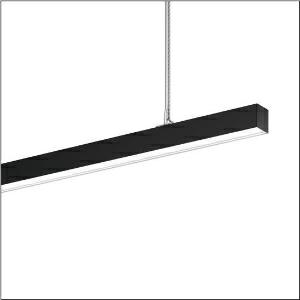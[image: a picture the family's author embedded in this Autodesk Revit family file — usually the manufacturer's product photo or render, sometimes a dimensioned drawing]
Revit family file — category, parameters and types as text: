
# Revit family: silica_r__21_51mx30da44bb_2b52
name_source: partatom
category: Lighting Fixtures
units: mm (PartAtom-declared; Revit-internal decimal feet)

## family parameters
Cut with Voids When Loaded = No
Host = Face
Light Source = No
Part Type = Normal
Room Calculation Point = No
Round Connector Dimension = Use Diameter
Shared = No

## types (1)
- --- (1 x LED, 4210 lm, 26 W, 4000K)
    Apparent Load = 26 VA
    CIE Flux Codes = 47 79 96 57 100
    Color Rendering = 80
    Color Temperature = 4000K
    Default Elevation = 1800 mm
    Description = Silica® 21, office luminaire, primary optical cover: cover, of PMMA, opal, light emission: direct/indirect distribution, primary light characteristic: symmetric, installation type: suspended mounting, LED, rated luminous flux: 4.210lm, luminous efficacy: 162lm/W, light colour: 840, colour temperature: 4000K, with terminal, 3+2-pole, max. 2.5mm², mains connection: 220..240V, AC, 50/60Hz, rated input power: 26W, luminaire housing, of aluminium, jet black (RAL 9005), length: 1.204mm, width: 53mm, height: 53mm, protection rating (complete): IP20, insulation class (complete): insulation class I (protective earthing), certification: CE, permissible operating ambient temperature: 0..+35°C, standard: EN 50419, packaging unit: 1 piece
    Height = 53 mm
    Lamp = 1 x LED
    Lamp Light Flux = 4210 lm
    Lamp Power = 26 W
    Lamp count = 1
    Length = 1204 mm
    Luminous efficacy = 162 lm/W
    Manufacturer = Siteco
    ModVariant = No
    Model = 51MX30DA44BB
    Mounting Place = Ceiling
    Mounting Type = Pendant
    Number of Poles = 1
    OnlyDefault = Yes
    Power Factor = 1
    Product Name = Silica® 21
    Product group = office luminaire | ceiling pendant
    ProductGroupID = 902
    Protection Class = Protection class I
    Protection Degree = IP 20
    RLX_Detail_Level = 1
    RLX_Emergency_Light_Flux = 0 lm
    RLX_Emergency_Type = 0
    RLX_Emergency_Type_DB = No
    RlxData = <blob elided: 25745 chars, md5=c354ed7e>
    Socket = socket
    Standby Power = 0 W
    System Light Flux = 4210 lm
    System Power = 26 W
    Type Comments = factory setting: luminous flux: 100 % | dim-lin: 254 | 218 mA
    Type Image = l_1335856.jpg
    URL = http://relux.com
    VarID = @adj_086197
    Voltage = 0 V
    Weight = 0.00 kg
    Width = 53 mm

## geometry (parser evidence)
native form markers: Blend x4, Sweep x11
no freeform markers — native parametric forms only
